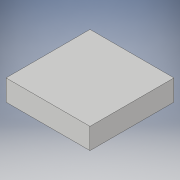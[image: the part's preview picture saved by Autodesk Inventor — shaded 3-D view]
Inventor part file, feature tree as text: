
AUTODESK INVENTOR PART (.ipt)
format: ipt  version: 2019 (Build 230136000, 136)  size: 207,872 bytes
history: native  units: mm
features: extrude x1, sketch x1
ambient origin geometry x8: Origin, YZ Plane, XZ Plane, XY Plane, X Axis, Y Axis, Z Axis, Center Point
bodies: Solid1 (feature_tree)
feature tree (2):
  extrude  "Extrusion1"  Depth=20.0mm
  sketch  "Sketch1"  dims[d0=20.0mm d1=20.0mm d2=5.0mm d3=0.0mm]
